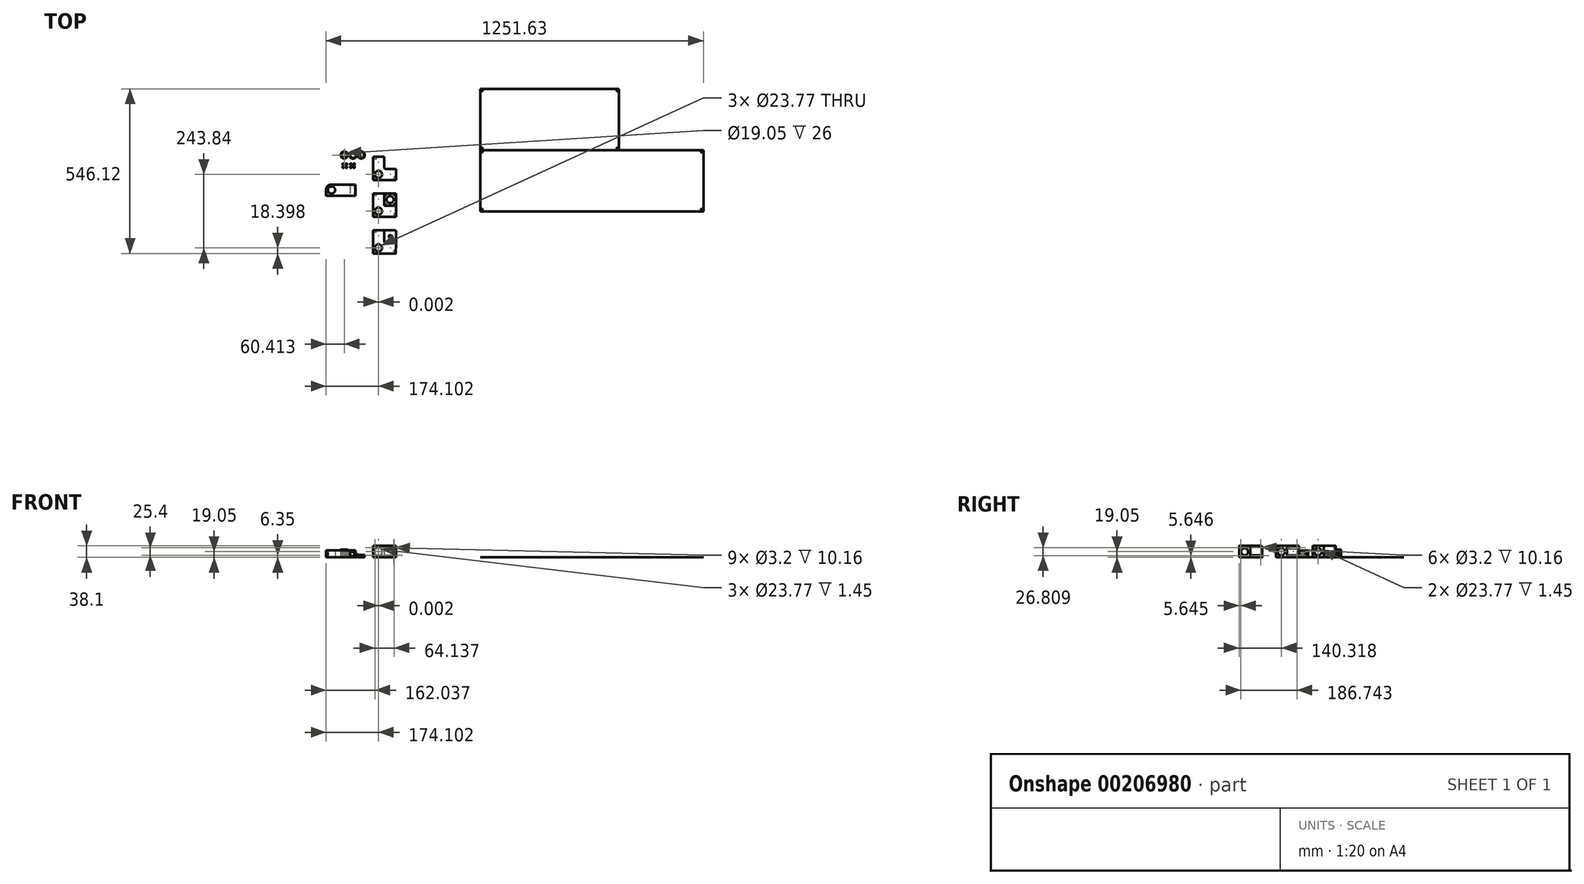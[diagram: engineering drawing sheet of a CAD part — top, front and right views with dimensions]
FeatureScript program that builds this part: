
annotation { "Feature Type Name" : "Feature", "Feature Type Description" : "" }
export const myFeature = defineFeature(function(context is Context, id is Id, definition is map)
    precondition{}
    {
        {
            assignVariable(context, id + "F0", {"name" : "frame_width", "anyValue" : 26});
        }
        {
            assignVariable(context, id + "F1", {"name" : "frame_depth", "anyValue" : 15});
        }
        {
            assignVariable(context, id + "F2", {"name" : "frame_height", "anyValue" : 8});
        }
        {
            assignVariable(context, id + "F3", {"name" : "recess", "anyValue" : 1.45});
        }
        {
            assignVariable(context, id + "F4", {"name" : "panel_thickness", "anyValue" : 0.12});
        }
        {
            var Q0;
            Q0=qCreatedBy(makeId("Top.planeOp"),FACE);
            var sketch = newSketch(context, id + "F5", { "sketchPlane" : qUnion([Q0])});
            skCircle(sketch, "E0", {"center": v(-63.66, 41.37) * mm, "radius": 11.89 * mm});
            skCircle(sketch, "E1", {"center": v(-63.66, 41.37) * mm, "radius": 9.53 * mm});
            skCircle(sketch, "E2", {"center": v(-34.26, 41.37) * mm, "radius": 11.89 * mm});
            skCircle(sketch, "E3", {"center": v(-34.26, 41.37) * mm, "radius": 9.53 * mm});
            skCircle(sketch, "E4", {"center": v(-7.3, 41.37) * mm, "radius": 11.89 * mm});
            skCircle(sketch, "E5", {"center": v(-7.3, 41.37) * mm, "radius": 9.53 * mm});
            skSolve(sketch);
        }
        {
            var Q0;
            Q0=makeQuery(id+"F5.imprint","IMPRINT",FACE,{"disambiguationData":[TD([[makeQuery(id+"F5.imprint","IMPRINT",EDGE,{"derivedFrom":sQuery(id+"F5.wireOp",EDGE,"E0")}),1.0]])]});
            extrude(context, id + "F6", {"entities" : qUnion([Q0]), "depth" : (getVariable(context, 'frame_width')) * mm});
        }
        {
            var Q0;
            Q0=makeQuery(id+"F5.imprint","IMPRINT",FACE,{"disambiguationData":[TD([[makeQuery(id+"F5.imprint","IMPRINT",EDGE,{"derivedFrom":sQuery(id+"F5.wireOp",EDGE,"E2")}),1.0]])]});
            extrude(context, id + "F7", {"entities" : qUnion([Q0]), "depth" : (getVariable(context, 'frame_depth')) * mm});
        }
        {
            var Q0;
            Q0=makeQuery(id+"F5.imprint","IMPRINT",FACE,{"disambiguationData":[TD([[makeQuery(id+"F5.imprint","IMPRINT",EDGE,{"derivedFrom":sQuery(id+"F5.wireOp",EDGE,"E4")}),1.0]])]});
            extrude(context, id + "F8", {"entities" : qUnion([Q0]), "depth" : (getVariable(context, 'frame_height')) * mm});
        }
        {
            var Q0;
            Q0=qCreatedBy(makeId("Top.planeOp"),FACE);
            var sketch = newSketch(context, id + "F9", { "sketchPlane" : qUnion([Q0])});
            skLineSegment(sketch, "E6.bottom", {"start": v(-69.24, 13.5) * mm, "end": v(-63.96, 13.5) * mm});
            skLineSegment(sketch, "E6.left", {"start": v(-69.24, 13.5) * mm, "end": v(-69.24, 8.21) * mm});
            skLineSegment(sketch, "E6.right", {"start": v(-54.24, 13.5) * mm, "end": v(-54.24, 8.21) * mm});
            skLineSegment(sketch, "E7", {"start": v(-61.74, 13.5) * mm, "end": v(-61.74, -1.5) * mm, "construction": true});
            skLineSegment(sketch, "E8", {"start": v(-54.24, 6) * mm, "end": v(-69.24, 6) * mm, "construction": true});
            skLineSegment(sketch, "E9", {"start": v(-63.96, 13.5) * mm, "end": v(-63.96, 9.94) * mm});
            skLineSegment(sketch, "E10", {"start": v(-63.96, 9.94) * mm, "end": v(-59.52, 9.94) * mm});
            skLineSegment(sketch, "E11", {"start": v(-59.52, 9.94) * mm, "end": v(-59.52, 13.5) * mm});
            skLineSegment(sketch, "E12", {"start": v(-63.96, 11.71) * mm, "end": v(-61.74, 11.71) * mm, "construction": true});
            skLineSegment(sketch, "E13", {"start": v(-61.74, 11.61) * mm, "end": v(-59.52, 11.61) * mm, "construction": true});
            skLineSegment(sketch, "E14.MirrorCS", {"start": v(-63.96, 0.27) * mm, "end": v(-61.74, 0.27) * mm, "construction": true});
            skLineSegment(sketch, "E15.MirrorCS", {"start": v(-61.74, 0.37) * mm, "end": v(-59.52, 0.37) * mm, "construction": true});
            skLineSegment(sketch, "E16.MirrorCS", {"start": v(-63.96, 2.05) * mm, "end": v(-59.52, 2.05) * mm});
            skLineSegment(sketch, "E17.MirrorCS", {"start": v(-59.52, 2.05) * mm, "end": v(-59.52, -1.5) * mm});
            skLineSegment(sketch, "E18.MirrorCS", {"start": v(-63.96, -1.5) * mm, "end": v(-63.96, 2.05) * mm});
            skLineSegment(sketch, "E19.trimOffspring", {"start": v(-61.74, -1.5) * mm, "end": v(-54.24, -1.5) * mm});
            skLineSegment(sketch, "E20.trimOffspring", {"start": v(-59.52, 13.5) * mm, "end": v(-54.24, 13.5) * mm});
            skLineSegment(sketch, "E21", {"start": v(-69.24, -1.5) * mm, "end": v(-63.96, -1.5) * mm});
            skLineSegment(sketch, "E22", {"start": v(-54.24, 8.21) * mm, "end": v(-57.8, 8.21) * mm});
            skLineSegment(sketch, "E23", {"start": v(-57.8, 8.21) * mm, "end": v(-57.8, 3.77) * mm});
            skLineSegment(sketch, "E24", {"start": v(-57.8, 3.77) * mm, "end": v(-54.24, 3.77) * mm});
            skLineSegment(sketch, "E25", {"start": v(-56.02, 8.21) * mm, "end": v(-56.02, 6) * mm, "construction": true});
            skLineSegment(sketch, "E26", {"start": v(-56.85, 3.77) * mm, "end": v(-56.85, 6) * mm, "construction": true});
            skLineSegment(sketch, "E27", {"start": v(-69.24, 8.21) * mm, "end": v(-65.68, 8.21) * mm});
            skLineSegment(sketch, "E28", {"start": v(-65.68, 8.21) * mm, "end": v(-65.68, 3.77) * mm});
            skLineSegment(sketch, "E29", {"start": v(-65.68, 3.77) * mm, "end": v(-69.24, 3.77) * mm});
            skLineSegment(sketch, "E30", {"start": v(-67.46, 3.77) * mm, "end": v(-67.46, 6) * mm, "construction": true});
            skLineSegment(sketch, "E31", {"start": v(-66.67, 8.21) * mm, "end": v(-66.67, 6) * mm, "construction": true});
            skLineSegment(sketch, "E32.trimOffspring", {"start": v(-69.24, 3.77) * mm, "end": v(-69.24, -1.5) * mm});
            skLineSegment(sketch, "E33.trimOffspring", {"start": v(-54.24, 3.77) * mm, "end": v(-54.24, -1.5) * mm});
            skCircle(sketch, "E34", {"center": v(-61.74, 6) * mm, "radius": 1.25 * mm});
            skLineSegment(sketch, "E35.1.0.0", {"start": v(-41.27, 8.21) * mm, "end": v(-41.27, 6) * mm, "construction": true});
            skLineSegment(sketch, "E35.1.0.1", {"start": v(-43.84, 8.21) * mm, "end": v(-40.28, 8.21) * mm});
            skLineSegment(sketch, "E35.1.0.2", {"start": v(-36.34, 0.37) * mm, "end": v(-34.12, 0.37) * mm, "construction": true});
            skLineSegment(sketch, "E35.1.0.3", {"start": v(-28.84, 13.5) * mm, "end": v(-28.84, 8.21) * mm});
            skLineSegment(sketch, "E35.1.0.4", {"start": v(-30.62, 8.21) * mm, "end": v(-30.62, 6) * mm, "construction": true});
            skLineSegment(sketch, "E35.1.0.5", {"start": v(-36.34, 11.61) * mm, "end": v(-34.12, 11.61) * mm, "construction": true});
            skLineSegment(sketch, "E35.1.0.6", {"start": v(-38.56, -1.5) * mm, "end": v(-38.56, 2.05) * mm});
            skLineSegment(sketch, "E35.1.0.7", {"start": v(-43.84, 3.77) * mm, "end": v(-43.84, -1.5) * mm});
            skLineSegment(sketch, "E35.1.0.8", {"start": v(-43.84, 13.5) * mm, "end": v(-38.56, 13.5) * mm});
            skLineSegment(sketch, "E35.1.0.9", {"start": v(-28.84, 6) * mm, "end": v(-43.84, 6) * mm, "construction": true});
            skLineSegment(sketch, "E35.1.0.10", {"start": v(-40.28, 3.77) * mm, "end": v(-43.84, 3.77) * mm});
            skLineSegment(sketch, "E35.1.0.11", {"start": v(-38.56, 0.27) * mm, "end": v(-36.34, 0.27) * mm, "construction": true});
            skLineSegment(sketch, "E35.1.0.12", {"start": v(-38.56, 13.5) * mm, "end": v(-38.56, 9.94) * mm});
            skLineSegment(sketch, "E35.1.0.13", {"start": v(-28.84, 8.21) * mm, "end": v(-32.4, 8.21) * mm});
            skLineSegment(sketch, "E35.1.0.14", {"start": v(-38.56, 11.71) * mm, "end": v(-36.34, 11.71) * mm, "construction": true});
            skLineSegment(sketch, "E35.1.0.15", {"start": v(-43.84, -1.5) * mm, "end": v(-38.56, -1.5) * mm});
            skLineSegment(sketch, "E35.1.0.16", {"start": v(-36.34, -1.5) * mm, "end": v(-28.84, -1.5) * mm});
            skLineSegment(sketch, "E35.1.0.17", {"start": v(-28.84, 3.77) * mm, "end": v(-28.84, -1.5) * mm});
            skLineSegment(sketch, "E35.1.0.18", {"start": v(-32.4, 3.77) * mm, "end": v(-28.84, 3.77) * mm});
            skLineSegment(sketch, "E35.1.0.19", {"start": v(-36.34, 13.5) * mm, "end": v(-36.34, -1.5) * mm, "construction": true});
            skLineSegment(sketch, "E35.1.0.20", {"start": v(-34.12, 9.94) * mm, "end": v(-34.12, 13.5) * mm});
            skLineSegment(sketch, "E35.1.0.21", {"start": v(-42.06, 3.77) * mm, "end": v(-42.06, 6) * mm, "construction": true});
            skLineSegment(sketch, "E35.1.0.22", {"start": v(-43.84, 13.5) * mm, "end": v(-43.84, 8.21) * mm});
            skLineSegment(sketch, "E35.1.0.23", {"start": v(-32.4, 8.21) * mm, "end": v(-32.4, 3.77) * mm});
            skCircle(sketch, "E35.1.0.24", {"center": v(-36.34, 6) * mm, "radius": 1.25 * mm});
            skLineSegment(sketch, "E35.1.0.25", {"start": v(-38.56, 9.94) * mm, "end": v(-34.12, 9.94) * mm});
            skLineSegment(sketch, "E35.1.0.26", {"start": v(-34.12, 13.5) * mm, "end": v(-28.84, 13.5) * mm});
            skLineSegment(sketch, "E35.1.0.27", {"start": v(-40.28, 8.21) * mm, "end": v(-40.28, 3.77) * mm});
            skLineSegment(sketch, "E35.1.0.28", {"start": v(-34.12, 2.05) * mm, "end": v(-34.12, -1.5) * mm});
            skLineSegment(sketch, "E35.1.0.29", {"start": v(-38.56, 2.05) * mm, "end": v(-34.12, 2.05) * mm});
            skLineSegment(sketch, "E35.1.0.30", {"start": v(-31.45, 3.77) * mm, "end": v(-31.45, 6) * mm, "construction": true});
            skLineSegment(sketch, "E35.direction1", {"start": v(-69.24, -1.5) * mm, "end": v(-43.84, -1.5) * mm, "construction": true});
            skSolve(sketch);
        }
        {
            var Q0;
            Q0=makeQuery(id+"F9.imprint","IMPRINT",FACE,{"disambiguationData":[TD([[makeQuery(id+"F9.imprint","IMPRINT",EDGE,{"derivedFrom":sQuery(id+"F9.wireOp",EDGE,"E6.bottom")}),-1.0]])]});
            extrude(context, id + "F10", {"entities" : qUnion([Q0]), "depth" : (getVariable(context, 'frame_width') - 4.5) * mm});
        }
        {
            var Q0;
            Q0=makeQuery(id+"F9.imprint","IMPRINT",FACE,{"disambiguationData":[TD([[makeQuery(id+"F9.imprint","IMPRINT",EDGE,{"derivedFrom":sQuery(id+"F9.wireOp",EDGE,"E35.1.0.1")}),1.0]])]});
            extrude(context, id + "F11", {"entities" : qUnion([Q0]), "depth" : (getVariable(context, 'frame_depth') + getVariable(context, 'recess') * 2.1) * mm});
        }
        {
            var Q0;
            Q0=makeQuery(id+"F10.opExtrude","SWEPT_EDGE",EDGE,{"disambiguationData":[OSD([sQuery(id+"F9.wireOp",EDGE,"E6.bottom"),sQuery(id+"F9.wireOp",EDGE,"E6.left")])]});
            var Q1;
            Q1=makeQuery(id+"F10.opExtrude","SWEPT_EDGE",EDGE,{"disambiguationData":[OSD([sQuery(id+"F9.wireOp",EDGE,"E6.right"),sQuery(id+"F9.wireOp",EDGE,"E20.trimOffspring")])]});
            var Q2;
            Q2=makeQuery(id+"F10.opExtrude","SWEPT_EDGE",EDGE,{"disambiguationData":[OSD([sQuery(id+"F9.wireOp",EDGE,"E19.trimOffspring"),sQuery(id+"F9.wireOp",EDGE,"E33.trimOffspring")])]});
            var Q3;
            Q3=makeQuery(id+"F10.opExtrude","SWEPT_EDGE",EDGE,{"disambiguationData":[OSD([sQuery(id+"F9.wireOp",EDGE,"E21"),sQuery(id+"F9.wireOp",EDGE,"E32.trimOffspring")])]});
            var Q4;
            Q4=makeQuery(id+"F11.opExtrude","SWEPT_EDGE",EDGE,{"disambiguationData":[OSD([sQuery(id+"F9.wireOp",EDGE,"E35.1.0.8"),sQuery(id+"F9.wireOp",EDGE,"E35.1.0.22")])]});
            var Q5;
            Q5=makeQuery(id+"F11.opExtrude","SWEPT_EDGE",EDGE,{"disambiguationData":[OSD([sQuery(id+"F9.wireOp",EDGE,"E35.1.0.3"),sQuery(id+"F9.wireOp",EDGE,"E35.1.0.26")])]});
            var Q6;
            Q6=makeQuery(id+"F11.opExtrude","SWEPT_EDGE",EDGE,{"disambiguationData":[OSD([sQuery(id+"F9.wireOp",EDGE,"E35.1.0.16"),sQuery(id+"F9.wireOp",EDGE,"E35.1.0.17")])]});
            var Q7;
            Q7=makeQuery(id+"F11.opExtrude","SWEPT_EDGE",EDGE,{"disambiguationData":[OSD([sQuery(id+"F9.wireOp",EDGE,"E35.1.0.7"),sQuery(id+"F9.wireOp",EDGE,"E35.1.0.15")])]});
            fillet(context, id + "F12", {"entities" : qUnion([Q0, Q1, Q2, Q3, Q4, Q5, Q6, Q7]), "radius" : 0.76 * mm, "tangentPropagation" : true, "allowEdgeOverflow" : false});
        }
        {
            var Q0;
            Q0=makeQuery(id+"F11.opExtrude","SWEPT_EDGE",EDGE,{"disambiguationData":[OSD([sQuery(id+"F9.wireOp",EDGE,"E35.1.0.20"),sQuery(id+"F9.wireOp",EDGE,"E35.1.0.25")])]});
            var Q1;
            Q1=makeQuery(id+"F10.opExtrude","SWEPT_EDGE",EDGE,{"disambiguationData":[OSD([sQuery(id+"F9.wireOp",EDGE,"E10"),sQuery(id+"F9.wireOp",EDGE,"E11")])]});
            var Q2;
            Q2=makeQuery(id+"F10.opExtrude","SWEPT_EDGE",EDGE,{"disambiguationData":[OSD([sQuery(id+"F9.wireOp",EDGE,"E9"),sQuery(id+"F9.wireOp",EDGE,"E10")])]});
            var Q3;
            Q3=makeQuery(id+"F10.opExtrude","SWEPT_EDGE",EDGE,{"disambiguationData":[OSD([sQuery(id+"F9.wireOp",EDGE,"E22"),sQuery(id+"F9.wireOp",EDGE,"E23")])]});
            var Q4;
            Q4=makeQuery(id+"F10.opExtrude","SWEPT_EDGE",EDGE,{"disambiguationData":[OSD([sQuery(id+"F9.wireOp",EDGE,"E23"),sQuery(id+"F9.wireOp",EDGE,"E24")])]});
            var Q5;
            Q5=makeQuery(id+"F10.opExtrude","SWEPT_EDGE",EDGE,{"disambiguationData":[OSD([sQuery(id+"F9.wireOp",EDGE,"E16.MirrorCS"),sQuery(id+"F9.wireOp",EDGE,"E17.MirrorCS")])]});
            var Q6;
            Q6=makeQuery(id+"F10.opExtrude","SWEPT_EDGE",EDGE,{"disambiguationData":[OSD([sQuery(id+"F9.wireOp",EDGE,"E16.MirrorCS"),sQuery(id+"F9.wireOp",EDGE,"E18.MirrorCS")])]});
            var Q7;
            Q7=makeQuery(id+"F10.opExtrude","SWEPT_EDGE",EDGE,{"disambiguationData":[OSD([sQuery(id+"F9.wireOp",EDGE,"E27"),sQuery(id+"F9.wireOp",EDGE,"E28")])]});
            var Q8;
            Q8=makeQuery(id+"F10.opExtrude","SWEPT_EDGE",EDGE,{"disambiguationData":[OSD([sQuery(id+"F9.wireOp",EDGE,"E28"),sQuery(id+"F9.wireOp",EDGE,"E29")])]});
            var Q9;
            Q9=makeQuery(id+"F11.opExtrude","SWEPT_EDGE",EDGE,{"disambiguationData":[OSD([sQuery(id+"F9.wireOp",EDGE,"E35.1.0.18"),sQuery(id+"F9.wireOp",EDGE,"E35.1.0.23")])]});
            var Q10;
            Q10=makeQuery(id+"F11.opExtrude","SWEPT_EDGE",EDGE,{"disambiguationData":[OSD([sQuery(id+"F9.wireOp",EDGE,"E35.1.0.13"),sQuery(id+"F9.wireOp",EDGE,"E35.1.0.23")])]});
            var Q11;
            Q11=makeQuery(id+"F11.opExtrude","SWEPT_EDGE",EDGE,{"disambiguationData":[OSD([sQuery(id+"F9.wireOp",EDGE,"E35.1.0.6"),sQuery(id+"F9.wireOp",EDGE,"E35.1.0.29")])]});
            var Q12;
            Q12=makeQuery(id+"F11.opExtrude","SWEPT_EDGE",EDGE,{"disambiguationData":[OSD([sQuery(id+"F9.wireOp",EDGE,"E35.1.0.28"),sQuery(id+"F9.wireOp",EDGE,"E35.1.0.29")])]});
            var Q13;
            Q13=makeQuery(id+"F11.opExtrude","SWEPT_EDGE",EDGE,{"disambiguationData":[OSD([sQuery(id+"F9.wireOp",EDGE,"E35.1.0.1"),sQuery(id+"F9.wireOp",EDGE,"E35.1.0.27")])]});
            var Q14;
            Q14=makeQuery(id+"F11.opExtrude","SWEPT_EDGE",EDGE,{"disambiguationData":[OSD([sQuery(id+"F9.wireOp",EDGE,"E35.1.0.10"),sQuery(id+"F9.wireOp",EDGE,"E35.1.0.27")])]});
            var Q15;
            Q15=makeQuery(id+"F11.opExtrude","SWEPT_EDGE",EDGE,{"disambiguationData":[OSD([sQuery(id+"F9.wireOp",EDGE,"E35.1.0.12"),sQuery(id+"F9.wireOp",EDGE,"E35.1.0.25")])]});
            fillet(context, id + "F13", {"entities" : qUnion([Q0, Q1, Q2, Q3, Q4, Q5, Q6, Q7, Q8, Q9, Q10, Q11, Q12, Q13, Q14, Q15]), "radius" : 1.27 * mm, "tangentPropagation" : true, "allowEdgeOverflow" : false});
        }
        {
            var Q0;
            Q0=qCreatedBy(makeId("Top.planeOp"),FACE);
            var sketch = newSketch(context, id + "F14", { "sketchPlane" : qUnion([Q0])});
            skArc(sketch, "E36", {"start": v(31.62, -22.94) * mm, "mid": v(37.01, -35.96) * mm, "end": v(50.03, -41.36) * mm});
            skCircle(sketch, "E37", {"center": v(50.03, -22.94) * mm, "radius": 11.89 * mm});
            skLineSegment(sketch, "E38.top", {"start": v(68.45, 35.48) * mm, "end": v(31.62, 35.48) * mm});
            skLineSegment(sketch, "E38.left", {"start": v(68.45, -4.53) * mm, "end": v(68.45, 35.48) * mm});
            skLineSegment(sketch, "E38.right", {"start": v(31.62, -22.94) * mm, "end": v(31.62, 35.48) * mm});
            skLineSegment(sketch, "E39.bottom", {"start": v(68.45, -4.53) * mm, "end": v(108.45, -4.53) * mm});
            skLineSegment(sketch, "E39.top", {"start": v(50.03, -41.36) * mm, "end": v(108.45, -41.36) * mm});
            skLineSegment(sketch, "E39.right", {"start": v(108.45, -4.53) * mm, "end": v(108.45, -41.36) * mm});
            skPoint(sketch, "E40.orphan", {"position": v(50.03, -4.53) * mm});
            skPoint(sketch, "E41.orphan", {"position": v(68.45, -22.94) * mm});
            skArc(sketch, "E42", {"start": v(31.62, -144.86) * mm, "mid": v(37.01, -157.88) * mm, "end": v(50.03, -163.28) * mm});
            skCircle(sketch, "E43", {"center": v(50.03, -144.86) * mm, "radius": 11.89 * mm});
            skLineSegment(sketch, "E44.top", {"start": v(68.45, -86.44) * mm, "end": v(31.62, -86.44) * mm});
            skLineSegment(sketch, "E44.left", {"start": v(68.45, -126.45) * mm, "end": v(68.45, -86.44) * mm});
            skLineSegment(sketch, "E44.right", {"start": v(31.62, -144.86) * mm, "end": v(31.62, -86.44) * mm});
            skLineSegment(sketch, "E45.bottom", {"start": v(68.45, -126.45) * mm, "end": v(108.45, -126.45) * mm});
            skLineSegment(sketch, "E45.top", {"start": v(50.03, -163.28) * mm, "end": v(108.45, -163.28) * mm});
            skLineSegment(sketch, "E45.right", {"start": v(108.45, -126.45) * mm, "end": v(108.45, -163.28) * mm});
            skPoint(sketch, "E46.orphan", {"position": v(50.03, -126.45) * mm});
            skPoint(sketch, "E47.orphan", {"position": v(68.45, -144.86) * mm});
            skLineSegment(sketch, "E48.top", {"start": v(68.45, -86.44) * mm, "end": v(108.45, -86.44) * mm});
            skLineSegment(sketch, "E48.right", {"start": v(108.45, -126.45) * mm, "end": v(108.45, -86.44) * mm});
            skCircle(sketch, "E49", {"center": v(88.45, -106.44) * mm, "radius": 11.75 * mm});
            skCircle(sketch, "E50", {"center": v(103.95, -90.94) * mm, "radius": 1.75 * mm});
            skCircle(sketch, "E51", {"center": v(103.95, -121.94) * mm, "radius": 1.75 * mm});
            skCircle(sketch, "E52", {"center": v(72.95, -121.94) * mm, "radius": 1.75 * mm});
            skCircle(sketch, "E53", {"center": v(72.95, -90.94) * mm, "radius": 1.75 * mm});
            skLineSegment(sketch, "E54", {"start": v(72.95, -90.94) * mm, "end": v(72.95, -121.94) * mm, "construction": true});
            skLineSegment(sketch, "E55", {"start": v(103.95, -121.94) * mm, "end": v(103.95, -90.94) * mm, "construction": true});
            skLineSegment(sketch, "E56", {"start": v(103.95, -90.94) * mm, "end": v(72.95, -90.94) * mm, "construction": true});
            skLineSegment(sketch, "E57", {"start": v(72.95, -121.94) * mm, "end": v(103.95, -121.94) * mm, "construction": true});
            skPoint(sketch, "E58", {"position": v(88.45, -90.94) * mm});
            skPoint(sketch, "E59", {"position": v(72.95, -106.44) * mm});
            skArc(sketch, "E60", {"start": v(31.62, -266.78) * mm, "mid": v(36.74, -279.52) * mm, "end": v(49.25, -285.18) * mm});
            skCircle(sketch, "E61", {"center": v(50.03, -266.78) * mm, "radius": 11.89 * mm});
            skLineSegment(sketch, "E62.top", {"start": v(68.45, -208.36) * mm, "end": v(31.62, -208.36) * mm});
            skLineSegment(sketch, "E62.left", {"start": v(68.45, -248.37) * mm, "end": v(68.45, -208.36) * mm});
            skLineSegment(sketch, "E62.right", {"start": v(31.62, -266.78) * mm, "end": v(31.62, -208.36) * mm});
            skLineSegment(sketch, "E63.bottom", {"start": v(68.45, -248.37) * mm, "end": v(108.45, -248.37) * mm});
            skLineSegment(sketch, "E63.top", {"start": v(49.25, -285.18) * mm, "end": v(107.34, -285.18) * mm});
            skLineSegment(sketch, "E63.right", {"start": v(108.45, -248.37) * mm, "end": v(107.34, -285.18) * mm});
            skPoint(sketch, "E64.orphan", {"position": v(50.03, -248.37) * mm});
            skPoint(sketch, "E65.orphan", {"position": v(68.45, -266.78) * mm});
            skLineSegment(sketch, "E66.top", {"start": v(68.45, -208.36) * mm, "end": v(108.45, -208.36) * mm});
            skLineSegment(sketch, "E66.right", {"start": v(108.45, -248.37) * mm, "end": v(108.45, -208.36) * mm});
            skCircle(sketch, "E67", {"center": v(88.45, -228.36) * mm, "radius": 4.33 * mm});
            skPoint(sketch, "E67.centerSnap0", {"position": v(88.45, -208.36) * mm});
            skPoint(sketch, "E68", {"position": v(68.45, -228.36) * mm});
            skLineSegment(sketch, "E69", {"start": v(103.95, -121.94) * mm, "end": v(103.95, -126.45) * mm, "construction": true});
            skLineSegment(sketch, "E70", {"start": v(103.95, -121.94) * mm, "end": v(108.45, -121.94) * mm, "construction": true});
            skLineSegment(sketch, "E71", {"start": v(72.95, -90.94) * mm, "end": v(68.45, -90.94) * mm, "construction": true});
            skLineSegment(sketch, "E72", {"start": v(31.62, -22.94) * mm, "end": v(31.62, -41.36) * mm});
            skLineSegment(sketch, "E73", {"start": v(31.62, -41.36) * mm, "end": v(50.03, -41.36) * mm});
            skLineSegment(sketch, "E74", {"start": v(31.62, -144.86) * mm, "end": v(31.62, -163.28) * mm});
            skLineSegment(sketch, "E75", {"start": v(31.62, -163.28) * mm, "end": v(50.03, -163.28) * mm});
            skLineSegment(sketch, "E76", {"start": v(31.62, -266.78) * mm, "end": v(31.62, -285.18) * mm});
            skLineSegment(sketch, "E77", {"start": v(31.62, -285.18) * mm, "end": v(49.25, -285.18) * mm});
            skSolve(sketch);
        }
        {
            var Q0;
            Q0=makeQuery(id+"F14.imprint","IMPRINT",FACE,{"disambiguationData":[TD([[makeQuery(id+"F14.imprint","IMPRINT",EDGE,{"derivedFrom":sQuery(id+"F14.wireOp",EDGE,"E36")}),1.0]])]});
            var Q1;
            Q1=makeQuery(id+"F14.imprint","IMPRINT",FACE,{"disambiguationData":[TD([[makeQuery(id+"F14.imprint","IMPRINT",EDGE,{"derivedFrom":sQuery(id+"F14.wireOp",EDGE,"E42")}),1.0]])]});
            var Q2;
            Q2=makeQuery(id+"F14.imprint","IMPRINT",FACE,{"disambiguationData":[TD([[makeQuery(id+"F14.imprint","IMPRINT",EDGE,{"derivedFrom":sQuery(id+"F14.wireOp",EDGE,"E60")}),1.0]])]});
            var Q3;
            Q3=makeQuery(id+"F14.imprint","IMPRINT",FACE,{"disambiguationData":[TD([[makeQuery(id+"F14.imprint","IMPRINT",EDGE,{"derivedFrom":sQuery(id+"F14.wireOp",EDGE,"E36")}),-1.0]])]});
            var Q4;
            Q4=makeQuery(id+"F14.imprint","IMPRINT",FACE,{"disambiguationData":[TD([[makeQuery(id+"F14.imprint","IMPRINT",EDGE,{"derivedFrom":sQuery(id+"F14.wireOp",EDGE,"E42")}),-1.0]])]});
            var Q5;
            Q5=makeQuery(id+"F14.imprint","IMPRINT",FACE,{"disambiguationData":[TD([[makeQuery(id+"F14.imprint","IMPRINT",EDGE,{"derivedFrom":sQuery(id+"F14.wireOp",EDGE,"E60")}),-1.0]])]});
            extrude(context, id + "F15", {"entities" : qUnion([Q0, Q1, Q2, Q3, Q4, Q5]), "depth" : 38.1 * mm});
        }
        {
            var Q0;
            Q0=makeQuery(id+"F15.opExtrude","SWEPT_EDGE",EDGE,{"disambiguationData":[OSD([sQuery(id+"F14.wireOp",EDGE,"E38.left"),sQuery(id+"F14.wireOp",EDGE,"E39.bottom")])]});
            fillet(context, id + "F16", {"entities" : qUnion([Q0]), "radius" : 5.08 * mm, "tangentPropagation" : true, "allowEdgeOverflow" : false});
        }
        {
            var Q0;
            Q0=makeQuery(id+"F15.opExtrude","SWEPT_FACE",FACE,{"disambiguationData":[OSD([sQuery(id+"F14.wireOp",EDGE,"E39.right")])]});
            var sketch = newSketch(context, id + "F17", { "sketchPlane" : qUnion([Q0])});
            skLineSegment(sketch, "E78.0", {"start": v(-4.53, 38.1) * mm, "end": v(-41.36, 38.1) * mm});
            skLineSegment(sketch, "E79.0", {"start": v(-41.36, 38.1) * mm, "end": v(-41.36, 0) * mm});
            skCircle(sketch, "E80", {"center": v(-22.94, 19.05) * mm, "radius": 11.89 * mm});
            skPoint(sketch, "E80.centerSnap0", {"position": v(-22.94, 38.1) * mm});
            skPoint(sketch, "E80.centerSnap1", {"position": v(-41.36, 19.05) * mm});
            skPoint(sketch, "E81.0", {"position": v(-163.28, 19.05) * mm});
            skPoint(sketch, "E82.0", {"position": v(-285.18, 19.05) * mm});
            skPoint(sketch, "E83.0", {"position": v(-266.77, 38.1) * mm});
            skCircle(sketch, "E84", {"center": v(-144.86, 19.05) * mm, "radius": 11.89 * mm});
            skCircle(sketch, "E85", {"center": v(-266.77, 19.05) * mm, "radius": 11.89 * mm});
            skPoint(sketch, "E86.0", {"position": v(-144.86, 38.1) * mm});
            skSolve(sketch);
        }
        {
            var Q0;
            Q0=makeQuery(id+"F15.opExtrude","SWEPT_FACE",FACE,{"disambiguationData":[OSD([sQuery(id+"F14.wireOp",EDGE,"E38.top")])]});
            var sketch = newSketch(context, id + "F18", { "sketchPlane" : qUnion([Q0])});
            skLineSegment(sketch, "E87.0", {"start": v(-68.45, 38.1) * mm, "end": v(-31.62, 38.1) * mm});
            skLineSegment(sketch, "E88.0", {"start": v(-31.62, 38.1) * mm, "end": v(-31.62, 0) * mm});
            skCircle(sketch, "E89", {"center": v(-50.03, 19.05) * mm, "radius": 11.89 * mm});
            skPoint(sketch, "E89.centerSnap0", {"position": v(-31.62, 19.05) * mm});
            skPoint(sketch, "E89.centerSnap1", {"position": v(-50.03, 38.1) * mm});
            skSolve(sketch);
        }
        {
            var Q0;
            Q0=makeQuery(id+"F17.imprint","IMPRINT",FACE,{"disambiguationData":[TD([[makeQuery(id+"F17.imprint","IMPRINT",EDGE,{"derivedFrom":sQuery(id+"F17.wireOp",EDGE,"E80")}),1.0]])]});
            var Q1;
            Q1=makeQuery(id+"F17.imprint","IMPRINT",FACE,{"disambiguationData":[TD([[makeQuery(id+"F17.imprint","IMPRINT",EDGE,{"derivedFrom":sQuery(id+"F17.wireOp",EDGE,"E85")}),1.0]])]});
            var Q2;
            Q2=makeQuery(id+"F17.imprint","IMPRINT",FACE,{"disambiguationData":[TD([[makeQuery(id+"F17.imprint","IMPRINT",EDGE,{"derivedFrom":sQuery(id+"F17.wireOp",EDGE,"E84")}),1.0]])]});
            extrude(context, id + "F19", {"entities" : qUnion([Q0, Q1, Q2]), "operationType" : NewBodyOperationType.REMOVE, "oppositeDirection" : true, "depth" : (getVariable(context, 'recess')) * mm});
        }
        {
            var Q0;
            Q0=makeQuery(id+"F18.imprint","IMPRINT",FACE,{"disambiguationData":[TD([[makeQuery(id+"F18.imprint","IMPRINT",EDGE,{"derivedFrom":sQuery(id+"F18.wireOp",EDGE,"E89")}),1.0]])]});
            extrude(context, id + "F20", {"entities" : qUnion([Q0]), "operationType" : NewBodyOperationType.REMOVE, "oppositeDirection" : true, "depth" : (getVariable(context, 'recess')) * mm});
        }
        {
            var Q0;
            {var subQ2=sQuery(id+"F14.wireOp",EDGE,"E48.top");Q0=makeQuery(id+"F14.imprint","IMPRINT",FACE,{"disambiguationData":[TD([[makeQuery(id+"F14.imprint","IMPRINT",EDGE,{"derivedFrom":subQ2}),-1.0]])]});}
            var Q1;
            Q1=makeQuery(id+"F14.imprint","IMPRINT",FACE,{"disambiguationData":[TD([[makeQuery(id+"F14.imprint","IMPRINT",EDGE,{"derivedFrom":sQuery(id+"F14.wireOp",EDGE,"E63.bottom")}),1.0]])]});
            extrude(context, id + "F21", {"entities" : qUnion([Q0, Q1]), "operationType" : NewBodyOperationType.ADD, "depth" : 6.35 * mm});
        }
        {
            var Q0;
            Q0=makeQuery(id+"F21.boolean.opBoolean","MERGE",FACE,{"derivedFrom":[makeQuery(id+"F15.opExtrude","SWEPT_FACE",FACE,{"disambiguationData":[OSD([sQuery(id+"F14.wireOp",EDGE,"E62.top")])]}),makeQuery(id+"F21.opExtrude","SWEPT_FACE",FACE,{"disambiguationData":[OSD([sQuery(id+"F14.wireOp",EDGE,"E66.top")])]})]});
            var sketch = newSketch(context, id + "F22", { "sketchPlane" : qUnion([Q0])});
            skCircle(sketch, "E90", {"center": v(-50.03, 19.05) * mm, "radius": 11.89 * mm});
            skPoint(sketch, "E90.centerSnap0", {"position": v(-31.62, 19.05) * mm});
            skPoint(sketch, "E91", {"position": v(-50.03, 38.1) * mm});
            skSolve(sketch);
        }
        {
            var Q0;
            Q0 = qSketchRegion(id + "F22", true);
            extrude(context, id + "F23", {"entities" : qUnion([Q0]), "operationType" : NewBodyOperationType.REMOVE, "oppositeDirection" : true, "depth" : (getVariable(context, 'recess')) * mm});
        }
        {
            var Q0;
            Q0=makeQuery(id+"F21.boolean.opBoolean","MERGE",FACE,{"derivedFrom":[makeQuery(id+"F15.opExtrude","SWEPT_FACE",FACE,{"disambiguationData":[OSD([sQuery(id+"F14.wireOp",EDGE,"E44.top")])]}),makeQuery(id+"F21.opExtrude","SWEPT_FACE",FACE,{"disambiguationData":[OSD([sQuery(id+"F14.wireOp",EDGE,"E48.top")])]})]});
            var sketch = newSketch(context, id + "F24", { "sketchPlane" : qUnion([Q0])});
            skCircle(sketch, "E92", {"center": v(-50.03, 19.05) * mm, "radius": 11.89 * mm});
            skPoint(sketch, "E92.centerSnap0", {"position": v(-31.62, 19.05) * mm});
            skPoint(sketch, "E93", {"position": v(-50.03, 38.1) * mm});
            skSolve(sketch);
        }
        {
            var Q0;
            Q0 = qSketchRegion(id + "F24", true);
            extrude(context, id + "F25", {"entities" : qUnion([Q0]), "operationType" : NewBodyOperationType.REMOVE, "oppositeDirection" : true, "depth" : (getVariable(context, 'recess')) * mm});
        }
        {
            var Q0;
            Q0=makeQuery(id+"F21.opExtrude","CAP_EDGE",EDGE,{"disambiguationData":[OSD([sQuery(id+"F14.wireOp",EDGE,"E66.right")])],"isStart":false});
            var Q1;
            Q1=makeQuery(id+"F21.opExtrude","CAP_EDGE",EDGE,{"disambiguationData":[OSD([sQuery(id+"F14.wireOp",EDGE,"E66.top")])],"isStart":false});
            var Q2;
            Q2=makeQuery(id+"F21.opExtrude","SWEPT_EDGE",EDGE,{"disambiguationData":[OSD([sQuery(id+"F14.wireOp",EDGE,"E66.top"),sQuery(id+"F14.wireOp",EDGE,"E66.right")])]});
            var Q3;
            Q3=makeQuery(id+"F15.opExtrude","SWEPT_EDGE",EDGE,{"disambiguationData":[OSD([sQuery(id+"F14.wireOp",EDGE,"E63.bottom"),sQuery(id+"F14.wireOp",EDGE,"E62.left")])]});
            var Q4;
            Q4=makeQuery(id+"F15.opExtrude","CAP_EDGE",EDGE,{"disambiguationData":[OSD([sQuery(id+"F14.wireOp",EDGE,"E63.bottom")])],"isStart":false});
            var Q5;
            Q5=makeQuery(id+"F15.opExtrude","CAP_EDGE",EDGE,{"disambiguationData":[OSD([sQuery(id+"F14.wireOp",EDGE,"E62.left")])],"isStart":false});
            var Q6;
            Q6=makeQuery(id+"F15.opExtrude","CAP_EDGE",EDGE,{"disambiguationData":[OSD([sQuery(id+"F14.wireOp",EDGE,"E62.top")])],"isStart":false});
            var Q7;
            Q7=makeQuery(id+"F15.opExtrude","SWEPT_EDGE",EDGE,{"disambiguationData":[OSD([sQuery(id+"F14.wireOp",EDGE,"E62.top"),sQuery(id+"F14.wireOp",EDGE,"E66.top"),sQuery(id+"F14.wireOp",EDGE,"E62.left")])]});
            var Q8;
            Q8=makeQuery(id+"F15.opExtrude","CAP_EDGE",EDGE,{"disambiguationData":[OSD([sQuery(id+"F14.wireOp",EDGE,"E63.right")])],"isStart":false});
            var Q9;
            Q9=makeQuery(id+"F15.opExtrude","SWEPT_FACE",FACE,{"disambiguationData":[OSD([sQuery(id+"F14.wireOp",EDGE,"E63.bottom")])]});
            var Q10;
            Q10=makeQuery(id+"F15.opExtrude","SWEPT_EDGE",EDGE,{"disambiguationData":[OSD([sQuery(id+"F14.wireOp",EDGE,"E45.bottom"),sQuery(id+"F14.wireOp",EDGE,"E44.left")])]});
            var Q11;
            Q11=makeQuery(id+"F15.opExtrude","CAP_EDGE",EDGE,{"disambiguationData":[OSD([sQuery(id+"F14.wireOp",EDGE,"E45.bottom")])],"isStart":false});
            var Q12;
            Q12=makeQuery(id+"F15.opExtrude","CAP_EDGE",EDGE,{"disambiguationData":[OSD([sQuery(id+"F14.wireOp",EDGE,"E45.right")])],"isStart":false});
            var Q13;
            Q13=makeQuery(id+"F21.boolean.opBoolean","SPLIT",EDGE,{"derivedFrom":makeQuery(id+"F15.opExtrude","SWEPT_EDGE",EDGE,{"disambiguationData":[OSD([sQuery(id+"F14.wireOp",EDGE,"E45.right"),sQuery(id+"F14.wireOp",EDGE,"E45.bottom"),sQuery(id+"F14.wireOp",EDGE,"E48.right")])]})});
            var Q14;
            Q14=makeQuery(id+"F15.opExtrude","SWEPT_EDGE",EDGE,{"disambiguationData":[OSD([sQuery(id+"F14.wireOp",EDGE,"E44.top"),sQuery(id+"F14.wireOp",EDGE,"E48.top"),sQuery(id+"F14.wireOp",EDGE,"E44.left")])]});
            var Q15;
            Q15=makeQuery(id+"F21.opExtrude","SWEPT_EDGE",EDGE,{"disambiguationData":[OSD([sQuery(id+"F14.wireOp",EDGE,"E48.top"),sQuery(id+"F14.wireOp",EDGE,"E48.right")])]});
            var Q16;
            Q16=makeQuery(id+"F15.opExtrude","CAP_EDGE",EDGE,{"disambiguationData":[OSD([sQuery(id+"F14.wireOp",EDGE,"E44.top")])],"isStart":false});
            var Q17;
            Q17=makeQuery(id+"F21.opExtrude","CAP_EDGE",EDGE,{"disambiguationData":[OSD([sQuery(id+"F14.wireOp",EDGE,"E62.left")])],"isStart":false});
            fillet(context, id + "F26", {"entities" : qUnion([Q0, Q1, Q2, Q3, Q4, Q5, Q6, Q7, Q8, Q9, Q10, Q11, Q12, Q13, Q14, Q15, Q16, Q17]), "radius" : 3.8 * mm, "tangentPropagation" : true, "allowEdgeOverflow" : false});
        }
        {
            var Q0;
            Q0=makeQuery(id+"F15.opExtrude","SWEPT_FACE",FACE,{"disambiguationData":[OSD([sQuery(id+"F14.wireOp",EDGE,"E38.right"),sQuery(id+"F14.wireOp",EDGE,"E72")])]});
            var sketch = newSketch(context, id + "F27", { "sketchPlane" : qUnion([Q0])});
            skCircle(sketch, "E94", {"center": v(-29.13, 31.75) * mm, "radius": 1.37 * mm});
            skCircle(sketch, "E95", {"center": v(35, 31.75) * mm, "radius": 1.58 * mm});
            skCircle(sketch, "E96", {"center": v(35, 6.35) * mm, "radius": 1.6 * mm});
            skCircle(sketch, "E97", {"center": v(-29.13, 6.35) * mm, "radius": 2.12 * mm});
            skLineSegment(sketch, "E98", {"start": v(-29.13, 31.75) * mm, "end": v(-29.13, 38.1) * mm, "construction": true});
            skLineSegment(sketch, "E99", {"start": v(-29.13, 31.75) * mm, "end": v(-35.48, 31.75) * mm, "construction": true});
            skLineSegment(sketch, "E100", {"start": v(35, 6.35) * mm, "end": v(41.36, 6.35) * mm, "construction": true});
            skLineSegment(sketch, "E101", {"start": v(35, 6.35) * mm, "end": v(35, 0) * mm, "construction": true});
            skSolve(sketch);
        }
        {
            var Q0;
            Q0=makeQuery(id+"F15.opExtrude","SWEPT_FACE",FACE,{"disambiguationData":[OSD([sQuery(id+"F14.wireOp",EDGE,"E44.right"),sQuery(id+"F14.wireOp",EDGE,"E74")])]});
            var sketch = newSketch(context, id + "F28", { "sketchPlane" : qUnion([Q0])});
            skCircle(sketch, "E102", {"center": v(92.8, 31.75) * mm, "radius": 1.6 * mm});
            skCircle(sketch, "E103", {"center": v(156.93, 31.75) * mm, "radius": 1.6 * mm});
            skCircle(sketch, "E104", {"center": v(156.93, 6.35) * mm, "radius": 1.6 * mm});
            skCircle(sketch, "E105", {"center": v(92.8, 6.35) * mm, "radius": 1.6 * mm});
            skLineSegment(sketch, "E106", {"start": v(92.8, 31.75) * mm, "end": v(92.8, 38.1) * mm, "construction": true});
            skLineSegment(sketch, "E107", {"start": v(92.8, 31.75) * mm, "end": v(86.44, 31.75) * mm, "construction": true});
            skLineSegment(sketch, "E108", {"start": v(156.93, 6.35) * mm, "end": v(156.93, 0) * mm, "construction": true});
            skLineSegment(sketch, "E109", {"start": v(156.93, 6.35) * mm, "end": v(163.28, 6.35) * mm, "construction": true});
            skSolve(sketch);
        }
        {
            var Q0;
            Q0=makeQuery(id+"F15.opExtrude","SWEPT_FACE",FACE,{"disambiguationData":[OSD([sQuery(id+"F14.wireOp",EDGE,"E62.right"),sQuery(id+"F14.wireOp",EDGE,"E76")])]});
            var sketch = newSketch(context, id + "F29", { "sketchPlane" : qUnion([Q0])});
            skCircle(sketch, "E110", {"center": v(214, 32.45) * mm, "radius": 1.6 * mm});
            skCircle(sketch, "E111", {"center": v(214, 5.65) * mm, "radius": 1.6 * mm});
            skCircle(sketch, "E112", {"center": v(279.53, 5.65) * mm, "radius": 1.6 * mm});
            skCircle(sketch, "E113", {"center": v(279.53, 32.45) * mm, "radius": 1.6 * mm});
            skLineSegment(sketch, "E114", {"start": v(214, 32.45) * mm, "end": v(214, 38.1) * mm, "construction": true});
            skLineSegment(sketch, "E115", {"start": v(214, 32.45) * mm, "end": v(208.36, 32.45) * mm, "construction": true});
            skLineSegment(sketch, "E116", {"start": v(279.53, 5.65) * mm, "end": v(279.53, 0) * mm, "construction": true});
            skLineSegment(sketch, "E117", {"start": v(279.53, 5.65) * mm, "end": v(285.18, 5.65) * mm, "construction": true});
            skSolve(sketch);
        }
        {
            var Q0;
            Q0 = qSketchRegion(id + "F27", true);
            var Q1;
            Q1 = qSketchRegion(id + "F29", true);
            var Q2;
            Q2 = qSketchRegion(id + "F28", true);
            extrude(context, id + "F30", {"entities" : qUnion([Q0, Q1, Q2]), "operationType" : NewBodyOperationType.REMOVE, "oppositeDirection" : true, "depth" : 10.16 * mm});
        }
        {
            var Q0;
            Q0=makeQuery(id+"F15.opExtrude","SWEPT_FACE",FACE,{"disambiguationData":[OSD([sQuery(id+"F14.wireOp",EDGE,"E39.top"),sQuery(id+"F14.wireOp",EDGE,"E73")])]});
            var sketch = newSketch(context, id + "F31", { "sketchPlane" : qUnion([Q0])});
            skCircle(sketch, "E118", {"center": v(37.97, 31.75) * mm, "radius": 1.6 * mm});
            skLineSegment(sketch, "E119", {"start": v(37.97, 31.75) * mm, "end": v(31.62, 31.75) * mm, "construction": true});
            skLineSegment(sketch, "E120", {"start": v(37.97, 31.75) * mm, "end": v(37.97, 38.1) * mm, "construction": true});
            skCircle(sketch, "E121", {"center": v(102.1, 31.75) * mm, "radius": 1.6 * mm});
            skCircle(sketch, "E122", {"center": v(102.1, 6.35) * mm, "radius": 1.6 * mm});
            skCircle(sketch, "E123", {"center": v(37.97, 6.35) * mm, "radius": 1.6 * mm});
            skLineSegment(sketch, "E124", {"start": v(102.1, 6.35) * mm, "end": v(108.45, 6.35) * mm, "construction": true});
            skLineSegment(sketch, "E125", {"start": v(102.1, 6.35) * mm, "end": v(102.1, 0) * mm, "construction": true});
            skSolve(sketch);
        }
        {
            var Q0;
            Q0=makeQuery(id+"F15.opExtrude","SWEPT_FACE",FACE,{"disambiguationData":[OSD([sQuery(id+"F14.wireOp",EDGE,"E45.top"),sQuery(id+"F14.wireOp",EDGE,"E75")])]});
            var sketch = newSketch(context, id + "F32", { "sketchPlane" : qUnion([Q0])});
            skCircle(sketch, "E126", {"center": v(37.97, 31.75) * mm, "radius": 1.6 * mm});
            skCircle(sketch, "E127", {"center": v(37.97, 6.35) * mm, "radius": 1.6 * mm});
            skCircle(sketch, "E128", {"center": v(102.1, 31.75) * mm, "radius": 1.6 * mm});
            skCircle(sketch, "E129", {"center": v(102.1, 6.35) * mm, "radius": 1.6 * mm});
            skLineSegment(sketch, "E130", {"start": v(37.97, 31.75) * mm, "end": v(37.97, 38.1) * mm, "construction": true});
            skLineSegment(sketch, "E131", {"start": v(37.97, 31.75) * mm, "end": v(31.62, 31.75) * mm, "construction": true});
            skLineSegment(sketch, "E132", {"start": v(102.1, 6.35) * mm, "end": v(108.45, 6.35) * mm, "construction": true});
            skLineSegment(sketch, "E133", {"start": v(102.1, 6.35) * mm, "end": v(102.1, 0) * mm, "construction": true});
            skSolve(sketch);
        }
        {
            var Q0;
            Q0=makeQuery(id+"F15.opExtrude","SWEPT_FACE",FACE,{"disambiguationData":[OSD([sQuery(id+"F14.wireOp",EDGE,"E63.top"),sQuery(id+"F14.wireOp",EDGE,"E77")])]});
            var sketch = newSketch(context, id + "F33", { "sketchPlane" : qUnion([Q0])});
            skCircle(sketch, "E134", {"center": v(37.97, 31.75) * mm, "radius": 1.6 * mm});
            skCircle(sketch, "E135", {"center": v(37.97, 6.35) * mm, "radius": 1.6 * mm});
            skCircle(sketch, "E136", {"center": v(101, 6.35) * mm, "radius": 1.6 * mm});
            skCircle(sketch, "E137", {"center": v(101, 31.75) * mm, "radius": 1.6 * mm});
            skLineSegment(sketch, "E138", {"start": v(37.97, 31.75) * mm, "end": v(37.97, 38.1) * mm, "construction": true});
            skLineSegment(sketch, "E139", {"start": v(37.97, 31.75) * mm, "end": v(31.62, 31.75) * mm, "construction": true});
            skLineSegment(sketch, "E140", {"start": v(101, 6.35) * mm, "end": v(101, 0) * mm, "construction": true});
            skLineSegment(sketch, "E141", {"start": v(101, 6.35) * mm, "end": v(107.34, 6.35) * mm, "construction": true});
            skSolve(sketch);
        }
        {
            var Q0;
            Q0 = qSketchRegion(id + "F33", true);
            var Q1;
            Q1 = qSketchRegion(id + "F32", true);
            var Q2;
            Q2 = qSketchRegion(id + "F31", true);
            extrude(context, id + "F34", {"entities" : qUnion([Q0, Q1, Q2]), "operationType" : NewBodyOperationType.REMOVE, "oppositeDirection" : true, "depth" : 10.16 * mm});
        }
        {
            var Q0;
            Q0=qCreatedBy(makeId("Top.planeOp"),FACE);
            var sketch = newSketch(context, id + "F35", { "sketchPlane" : qUnion([Q0])});
            skArc(sketch, "E142", {"start": v(-116.12, -80.41) * mm, "mid": v(-94.72, -70.13) * mm, "end": v(-116.99, -78.38) * mm});
            skArc(sketch, "E143", {"start": v(-105.66, -56.36) * mm, "mid": v(-118.68, -61.75) * mm, "end": v(-124.07, -74.78) * mm});
            skLineSegment(sketch, "E144.bottom", {"start": v(-105.66, -56.36) * mm, "end": v(-25.65, -56.36) * mm});
            skLineSegment(sketch, "E144.top", {"start": v(-105.66, -93.2) * mm, "end": v(-25.65, -93.2) * mm});
            skLineSegment(sketch, "E144.right", {"start": v(-25.65, -56.36) * mm, "end": v(-25.65, -93.2) * mm});
            skLineSegment(sketch, "E145", {"start": v(-124.07, -74.78) * mm, "end": v(-124.07, -78.38) * mm});
            skLineSegment(sketch, "E146", {"start": v(-124.07, -93.2) * mm, "end": v(-105.66, -93.2) * mm});
            skLineSegment(sketch, "E147", {"start": v(-124.07, -78.38) * mm, "end": v(-116.99, -78.38) * mm});
            skLineSegment(sketch, "E148", {"start": v(-124.07, -80.41) * mm, "end": v(-116.12, -80.41) * mm});
            skLineSegment(sketch, "E149.trimOffspring", {"start": v(-124.07, -80.41) * mm, "end": v(-124.07, -93.2) * mm});
            skSolve(sketch);
        }
        {
            var Q0;
            Q0 = qSketchRegion(id + "F35", true);
            extrude(context, id + "F36", {"entities" : qUnion([Q0]), "depth" : 22.86 * mm});
        }
        {
            var Q0;
            Q0=makeQuery(id+"F36.opExtrude","SWEPT_FACE",FACE,{"disambiguationData":[OSD([sQuery(id+"F35.wireOp",EDGE,"E144.top"),sQuery(id+"F35.wireOp",EDGE,"E146")])]});
            var sketch = newSketch(context, id + "F37", { "sketchPlane" : qUnion([Q0])});
            skLineSegment(sketch, "E150.bottom", {"start": v(-44.6, 19) * mm, "end": v(-29.46, 19) * mm});
            skLineSegment(sketch, "E150.top", {"start": v(-44.6, 3.86) * mm, "end": v(-29.46, 3.85) * mm});
            skLineSegment(sketch, "E150.left", {"start": v(-44.6, 19) * mm, "end": v(-44.6, 3.86) * mm});
            skLineSegment(sketch, "E150.right", {"start": v(-29.46, 19) * mm, "end": v(-29.46, 3.85) * mm});
            skPoint(sketch, "E150.middle", {"position": v(-37.03, 11.43) * mm});
            skPoint(sketch, "E150.middle.positionSnap0", {"position": v(-25.65, 11.43) * mm});
            skPoint(sketch, "E150.centerSnap0", {"position": v(-25.65, 11.43) * mm});
            skPoint(sketch, "E151", {"position": v(-121.03, 11.43) * mm});
            skPoint(sketch, "E151.positionSnap0", {"position": v(-124.07, 11.43) * mm});
            skSolve(sketch);
        }
        {
            var Q0;
            Q0 = qSketchRegion(id + "F37", true);
            extrude(context, id + "F38", {"entities" : qUnion([Q0]), "operationType" : NewBodyOperationType.REMOVE, "endBound" : BoundingType.THROUGH_ALL, "oppositeDirection" : true, "depth" : 25.4 * mm});
        }
        {
            var Q0;
            Q0=sQuery(id+"F37.wireOp",VERTEX,"E151");
            var Q1;
            Q1=makeQuery(id+"F6.opExtrude","SWEPT_BODY",BODY,{"disambiguationData":[OSD([sQuery(id+"F5.wireOp",EDGE,"E0"),sQuery(id+"F5.wireOp",EDGE,"E1")])]});
            var Q2;
            Q2=makeQuery(id+"F36.opExtrude","SWEPT_BODY",BODY,{"disambiguationData":[OSD([sQuery(id+"F35.wireOp",EDGE,"E142"),sQuery(id+"F35.wireOp",EDGE,"E143"),sQuery(id+"F35.wireOp",EDGE,"E144.bottom"),sQuery(id+"F35.wireOp",EDGE,"E144.top"),sQuery(id+"F35.wireOp",EDGE,"E144.right"),sQuery(id+"F35.wireOp",EDGE,"E145"),sQuery(id+"F35.wireOp",EDGE,"E146"),sQuery(id+"F35.wireOp",EDGE,"E147"),sQuery(id+"F35.wireOp",EDGE,"E148"),sQuery(id+"F35.wireOp",EDGE,"E149.trimOffspring")])]});
            hole(context, id + "F39", {"style" : HoleStyle.C_BORE, "endStyle" : HoleEndStyle.THROUGH, "holeDiameter" : 3.3 * mm, "cBoreDiameter" : 6 * mm, "cBoreDepth" : 1.5 * mm, "locations" : qUnion([Q0]), "scope" : qUnion([Q1, Q2]), "isTappedThrough" : true});
        }
        {
            var Q0;
            Q0=makeQuery(id+"F36.opExtrude","SWEPT_FACE",FACE,{"disambiguationData":[OSD([sQuery(id+"F35.wireOp",EDGE,"E147")])]});
            cPlane(context, id + "F40", {"entities" : qUnion([Q0]), "cplaneType" : CPlaneType.OFFSET, "offset" : 3.8 * mm, "oppositeDirection" : true, "width" : 152.4 * mm, "height" : 152.4 * mm});
        }
        {
            var Q0;
            Q0=qCreatedBy(id+"F40.planeOp",FACE);
            var sketch = newSketch(context, id + "F41", { "sketchPlane" : qUnion([Q0])});
            skCircle(sketch, "E152.0", {"center": v(-121.03, 11.43) * mm, "radius": 1.65 * mm});
            skCircle(sketch, "E153.cCircle", {"center": v(-121.03, 11.43) * mm, "radius": 2.95 * mm, "construction": true});
            skLineSegment(sketch, "E153.0", {"start": v(-122.73, 14.38) * mm, "end": v(-119.32, 14.38) * mm});
            skLineSegment(sketch, "E153.1", {"start": v(-119.32, 14.38) * mm, "end": v(-117.62, 11.43) * mm});
            skLineSegment(sketch, "E153.2", {"start": v(-117.62, 11.43) * mm, "end": v(-119.32, 8.48) * mm});
            skLineSegment(sketch, "E153.3", {"start": v(-119.32, 8.48) * mm, "end": v(-122.73, 8.48) * mm});
            skLineSegment(sketch, "E153.4", {"start": v(-122.73, 8.48) * mm, "end": v(-124.43, 11.43) * mm});
            skLineSegment(sketch, "E153.5", {"start": v(-124.43, 11.43) * mm, "end": v(-122.73, 14.38) * mm});
            skPoint(sketch, "E153.0.midPoint", {"position": v(-121.03, 14.38) * mm});
            skLineSegment(sketch, "E154.0", {"start": v(-124.07, 22.86) * mm, "end": v(-116.99, 22.86) * mm});
            skSolve(sketch);
        }
        {
            var Q0;
            Q0 = qSketchRegion(id + "F41", true);
            extrude(context, id + "F42", {"entities" : qUnion([Q0]), "operationType" : NewBodyOperationType.REMOVE, "oppositeDirection" : true, "depth" : 25.4 * mm});
        }
        {
            var Q0;
            Q0=makeQuery(id+"F36.opExtrude","SWEPT_FACE",FACE,{"disambiguationData":[OSD([sQuery(id+"F35.wireOp",EDGE,"E144.right")])]});
            var sketch = newSketch(context, id + "F43", { "sketchPlane" : qUnion([Q0])});
            skPoint(sketch, "E155", {"position": v(-86.02, 11.43) * mm});
            skPoint(sketch, "E155.positionSnap0", {"position": v(-93.2, 11.43) * mm});
            skPoint(sketch, "E156", {"position": v(-63.53, 11.43) * mm});
            skPoint(sketch, "E156.positionSnap0", {"position": v(-56.36, 11.43) * mm});
            skLineSegment(sketch, "E157", {"start": v(-56.36, 11.43) * mm, "end": v(-63.53, 11.43) * mm, "construction": true});
            skLineSegment(sketch, "E158", {"start": v(-86.02, 11.43) * mm, "end": v(-93.2, 11.43) * mm, "construction": true});
            skSolve(sketch);
        }
        {
            var Q0;
            Q0=sQuery(id+"F43.wireOp",VERTEX,"E155");
            var Q1;
            Q1=sQuery(id+"F43.wireOp",VERTEX,"E156");
            var Q2;
            Q2=makeQuery(id+"F36.opExtrude","SWEPT_BODY",BODY,{"disambiguationData":[OSD([sQuery(id+"F35.wireOp",EDGE,"E142"),sQuery(id+"F35.wireOp",EDGE,"E143"),sQuery(id+"F35.wireOp",EDGE,"E144.bottom"),sQuery(id+"F35.wireOp",EDGE,"E144.top"),sQuery(id+"F35.wireOp",EDGE,"E144.right"),sQuery(id+"F35.wireOp",EDGE,"E145"),sQuery(id+"F35.wireOp",EDGE,"E146"),sQuery(id+"F35.wireOp",EDGE,"E147"),sQuery(id+"F35.wireOp",EDGE,"E148"),sQuery(id+"F35.wireOp",EDGE,"E149.trimOffspring")])]});
            hole(context, id + "F44", {"style" : HoleStyle.SIMPLE, "endStyle" : HoleEndStyle.BLIND, "holeDiameter" : 3.3 * mm, "holeDepth" : 12.7 * mm, "locations" : qUnion([Q0, Q1]), "scope" : qUnion([Q2])});
        }
        {
            var Q0;
            Q0=makeQuery(id+"F38.boolean.opBoolean","COPY",EDGE,{"derivedFrom":makeQuery(id+"F38.opExtrude","SWEPT_EDGE",EDGE,{"disambiguationData":[OSD([sQuery(id+"F37.wireOp",EDGE,"E150.bottom"),sQuery(id+"F37.wireOp",EDGE,"E150.left")])]})});
            var Q1;
            Q1=makeQuery(id+"F38.boolean.opBoolean","COPY",EDGE,{"derivedFrom":makeQuery(id+"F38.opExtrude","SWEPT_EDGE",EDGE,{"disambiguationData":[OSD([sQuery(id+"F37.wireOp",EDGE,"E150.top"),sQuery(id+"F37.wireOp",EDGE,"E150.left")])]})});
            var Q2;
            Q2=makeQuery(id+"F38.boolean.opBoolean","COPY",EDGE,{"derivedFrom":makeQuery(id+"F38.opExtrude","SWEPT_EDGE",EDGE,{"disambiguationData":[OSD([sQuery(id+"F37.wireOp",EDGE,"E150.top"),sQuery(id+"F37.wireOp",EDGE,"E150.right")])]})});
            var Q3;
            Q3=makeQuery(id+"F38.boolean.opBoolean","COPY",EDGE,{"derivedFrom":makeQuery(id+"F38.opExtrude","SWEPT_EDGE",EDGE,{"disambiguationData":[OSD([sQuery(id+"F37.wireOp",EDGE,"E150.bottom"),sQuery(id+"F37.wireOp",EDGE,"E150.right")])]})});
            fillet(context, id + "F45", {"entities" : qUnion([Q0, Q1, Q2, Q3]), "radius" : 1.27 * mm, "tangentPropagation" : true, "allowEdgeOverflow" : false});
        }
        {
            var Q0;
            Q0=qCreatedBy(makeId("Top.planeOp"),FACE);
            var sketch = newSketch(context, id + "F46", { "sketchPlane" : qUnion([Q0])});
            skLineSegment(sketch, "E159.bottom", {"start": v(387.15, 260.94) * mm, "end": v(848.16, 260.94) * mm});
            skLineSegment(sketch, "E159.top", {"start": v(387.15, 57.74) * mm, "end": v(848.16, 57.74) * mm});
            skLineSegment(sketch, "E159.left", {"start": v(387.15, 260.94) * mm, "end": v(387.15, 57.74) * mm});
            skLineSegment(sketch, "E159.right", {"start": v(848.16, 260.94) * mm, "end": v(848.16, 57.74) * mm});
            skCircle(sketch, "E160", {"center": v(393.5, 254.59) * mm, "radius": 1.6 * mm});
            skCircle(sketch, "E161", {"center": v(841.8, 254.59) * mm, "radius": 1.6 * mm});
            skCircle(sketch, "E162", {"center": v(841.8, 64.09) * mm, "radius": 1.6 * mm});
            skCircle(sketch, "E163", {"center": v(393.5, 64.09) * mm, "radius": 1.6 * mm});
            skLineSegment(sketch, "E164", {"start": v(393.5, 254.59) * mm, "end": v(393.5, 260.94) * mm, "construction": true});
            skLineSegment(sketch, "E165", {"start": v(393.5, 254.59) * mm, "end": v(387.15, 254.59) * mm, "construction": true});
            skLineSegment(sketch, "E166", {"start": v(841.8, 64.09) * mm, "end": v(841.8, 57.74) * mm, "construction": true});
            skLineSegment(sketch, "E167", {"start": v(841.8, 64.09) * mm, "end": v(848.16, 64.09) * mm, "construction": true});
            skLineSegment(sketch, "E168.bottom", {"start": v(387.15, 57.74) * mm, "end": v(1127.56, 57.74) * mm});
            skLineSegment(sketch, "E168.top", {"start": v(387.15, -145.46) * mm, "end": v(1127.56, -145.46) * mm});
            skLineSegment(sketch, "E168.left", {"start": v(387.15, 57.74) * mm, "end": v(387.15, -145.46) * mm});
            skLineSegment(sketch, "E168.right", {"start": v(1127.56, 57.74) * mm, "end": v(1127.56, -145.46) * mm});
            skCircle(sketch, "E169", {"center": v(393.5, 51.39) * mm, "radius": 1.6 * mm});
            skCircle(sketch, "E170", {"center": v(393.5, -139.11) * mm, "radius": 1.6 * mm});
            skCircle(sketch, "E171", {"center": v(1121.2, -139.11) * mm, "radius": 1.6 * mm});
            skCircle(sketch, "E172", {"center": v(1121.2, 51.39) * mm, "radius": 1.6 * mm});
            skLineSegment(sketch, "E173", {"start": v(393.5, 51.39) * mm, "end": v(393.5, 57.74) * mm, "construction": true});
            skLineSegment(sketch, "E174", {"start": v(393.5, 51.39) * mm, "end": v(387.15, 51.39) * mm, "construction": true});
            skLineSegment(sketch, "E175", {"start": v(1121.2, -139.11) * mm, "end": v(1127.56, -139.11) * mm, "construction": true});
            skPoint(sketch, "E175.endSnap0", {"position": v(1127.56, -43.86) * mm});
            skLineSegment(sketch, "E176", {"start": v(1121.2, -139.11) * mm, "end": v(1121.2, -145.46) * mm, "construction": true});
            skSolve(sketch);
        }
        {
            var Q0;
            Q0=makeQuery(id+"F46.imprint","IMPRINT",FACE,{"disambiguationData":[TD([[makeQuery(id+"F46.imprint","IMPRINT",EDGE,{"derivedFrom":sQuery(id+"F46.wireOp",EDGE,"E159.bottom")}),-1.0]])]});
            extrude(context, id + "F47", {"entities" : qUnion([Q0]), "depth" : (getVariable(context, 'panel_thickness')) * mm});
        }
        {
            var Q0;
            Q0=makeQuery(id+"F46.imprint","IMPRINT",FACE,{"disambiguationData":[TD([[makeQuery(id+"F46.imprint","IMPRINT",EDGE,{"derivedFrom":sQuery(id+"F46.wireOp",EDGE,"E168.bottom")}),-1.0]])]});
            extrude(context, id + "F48", {"entities" : qUnion([Q0]), "depth" : (getVariable(context, 'panel_thickness')) * mm});
        }
    });
